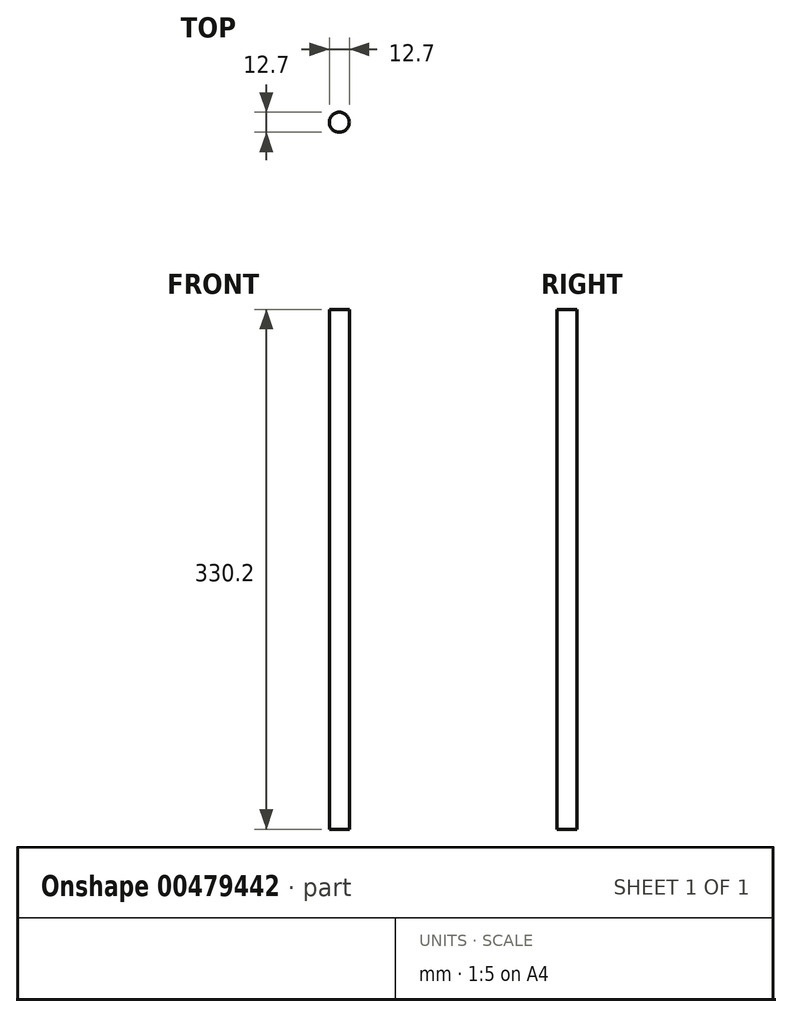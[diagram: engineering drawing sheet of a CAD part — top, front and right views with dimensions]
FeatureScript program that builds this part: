
annotation { "Feature Type Name" : "Feature", "Feature Type Description" : "" }
export const myFeature = defineFeature(function(context is Context, id is Id, definition is map)
    precondition{}
    {
        {
            var Q0;
            Q0=qCreatedBy(makeId("Top.planeOp"),FACE);
            var sketch = newSketch(context, id + "F0", { "sketchPlane" : qUnion([Q0])});
            skCircle(sketch, "E0", {"center": v(0, 0) * mm, "radius": 6.35 * mm});
            skSolve(sketch);
        }
        {
            var Q0;
            Q0 = qSketchRegion(id + "F0", true);
            extrude(context, id + "F1", {"entities" : qUnion([Q0]), "depth" : 330.2 * mm});
        }
    });
